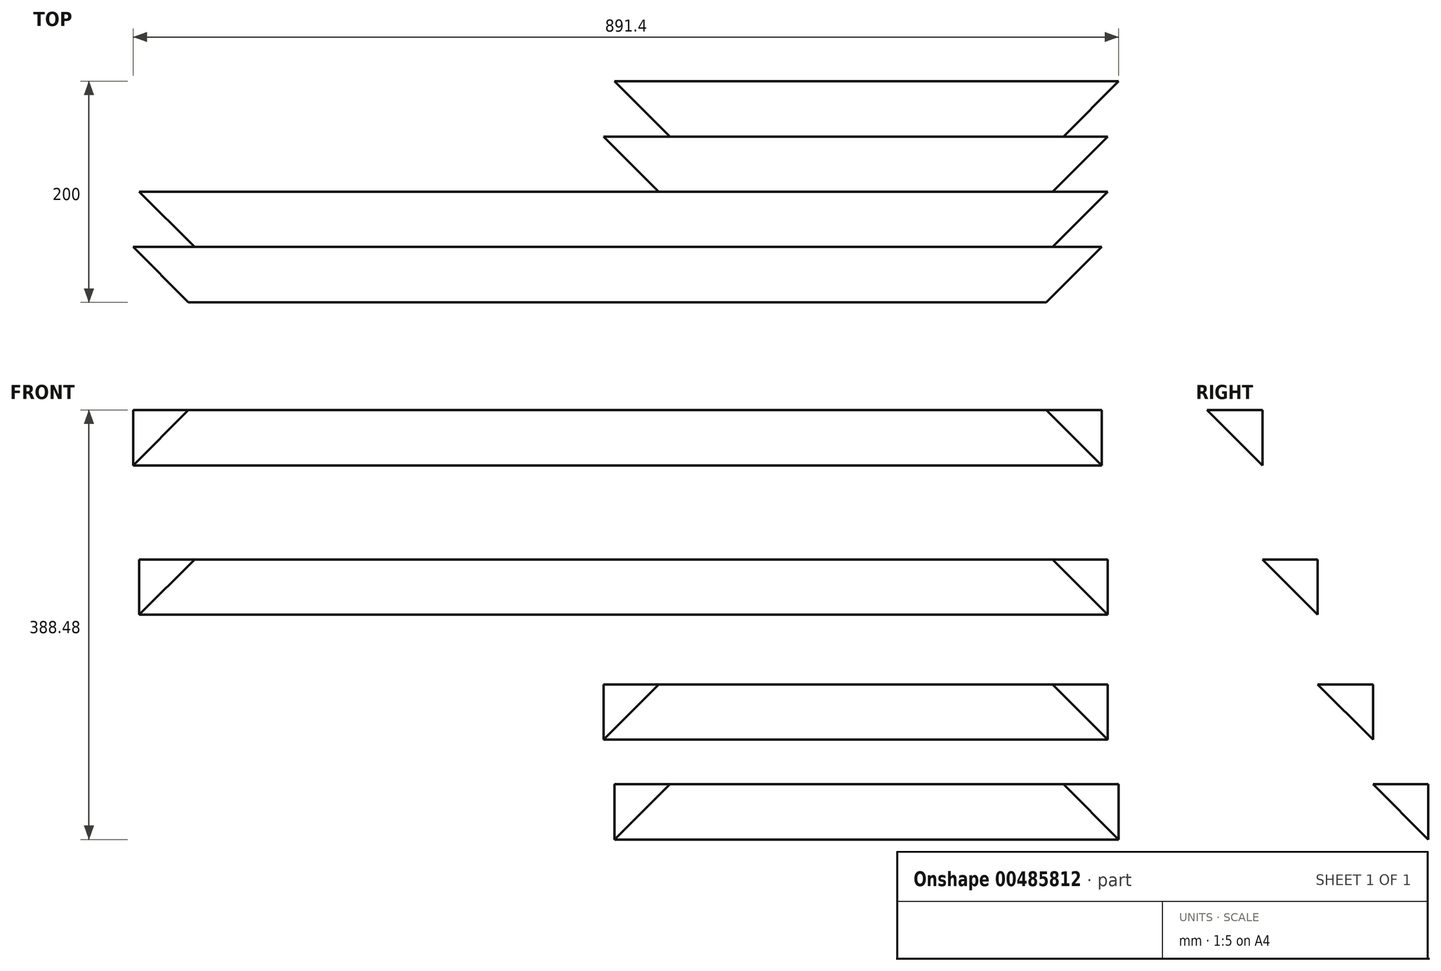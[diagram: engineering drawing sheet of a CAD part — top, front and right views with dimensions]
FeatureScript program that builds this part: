
annotation { "Feature Type Name" : "Feature", "Feature Type Description" : "" }
export const myFeature = defineFeature(function(context is Context, id is Id, definition is map)
    precondition{}
    {
        {
            var Q0;
            Q0=qCreatedBy(makeId("Top.planeOp"),FACE);
            var sketch = newSketch(context, id + "F0", { "sketchPlane" : qUnion([Q0])});
            skLineSegment(sketch, "E0.bottom", {"start": v(-271.54, 58.9) * mm, "end": v(604.46, 58.9) * mm});
            skLineSegment(sketch, "E0.top", {"start": v(-271.54, 8.9) * mm, "end": v(604.46, 8.9) * mm});
            skLineSegment(sketch, "E0.left", {"start": v(-271.54, 58.9) * mm, "end": v(-271.54, 8.9) * mm});
            skLineSegment(sketch, "E0.right", {"start": v(604.46, 58.9) * mm, "end": v(604.46, 8.9) * mm});
            skSolve(sketch);
        }
        {
            var Q0;
            Q0 = qSketchRegion(id + "F0", true);
            extrude(context, id + "F1", {"entities" : qUnion([Q0]), "depth" : 50 * mm});
        }
        {
            var Q0;
            Q0=makeQuery(id+"F1.opExtrude","SWEPT_FACE",FACE,{"disambiguationData":[OSD([sQuery(id+"F0.wireOp",EDGE,"E0.right")])]});
            var sketch = newSketch(context, id + "F2", { "sketchPlane" : qUnion([Q0])});
            skLineSegment(sketch, "E1", {"start": v(8.9, 50) * mm, "end": v(58.9, 0) * mm});
            skLineSegment(sketch, "E2", {"start": v(58.9, 0) * mm, "end": v(8.9, 0) * mm});
            skLineSegment(sketch, "E3", {"start": v(8.9, 0) * mm, "end": v(8.9, 50) * mm});
            skSolve(sketch);
        }
        {
            var Q0;
            Q0 = qSketchRegion(id + "F2", true);
            extrude(context, id + "F3", {"entities" : qUnion([Q0]), "operationType" : NewBodyOperationType.REMOVE, "endBound" : BoundingType.THROUGH_ALL, "oppositeDirection" : true, "depth" : 25 * mm});
        }
        {
            var Q0;
            Q0=makeQuery(id+"F1.opExtrude","SWEPT_FACE",FACE,{"disambiguationData":[OSD([sQuery(id+"F0.wireOp",EDGE,"E0.bottom")])]});
            var sketch = newSketch(context, id + "F4", { "sketchPlane" : qUnion([Q0])});
            skLineSegment(sketch, "E4.bottom", {"start": v(-609.99, -85.16) * mm, "end": v(266.01, -85.16) * mm});
            skLineSegment(sketch, "E4.top", {"start": v(-609.99, -135.16) * mm, "end": v(266.01, -135.16) * mm});
            skLineSegment(sketch, "E4.left", {"start": v(-609.99, -85.16) * mm, "end": v(-609.99, -135.16) * mm});
            skLineSegment(sketch, "E4.right", {"start": v(266.01, -85.16) * mm, "end": v(266.01, -135.16) * mm});
            skSolve(sketch);
        }
        {
            var Q0;
            Q0=makeQuery(id+"F4.imprint","IMPRINT",FACE,{"disambiguationData":[TD([[makeQuery(id+"F4.imprint","IMPRINT",EDGE,{"derivedFrom":sQuery(id+"F4.wireOp",EDGE,"E4.bottom")}),-1.0]])]});
            extrude(context, id + "F5", {"entities" : qUnion([Q0]), "depth" : 50 * mm});
        }
        {
            var Q0;
            Q0=makeQuery(id+"F5.opExtrude","SWEPT_FACE",FACE,{"disambiguationData":[OSD([sQuery(id+"F4.wireOp",EDGE,"E4.left")])]});
            var sketch = newSketch(context, id + "F6", { "sketchPlane" : qUnion([Q0])});
            skLineSegment(sketch, "E5", {"start": v(58.9, -85.16) * mm, "end": v(108.9, -135.16) * mm});
            skLineSegment(sketch, "E6", {"start": v(108.9, -135.16) * mm, "end": v(58.9, -135.16) * mm});
            skLineSegment(sketch, "E7", {"start": v(58.9, -135.16) * mm, "end": v(58.9, -85.16) * mm});
            skSolve(sketch);
        }
        {
            var Q0;
            Q0=makeQuery(id+"F6.imprint","IMPRINT",FACE,{"disambiguationData":[TD([[makeQuery(id+"F6.imprint","IMPRINT",EDGE,{"derivedFrom":sQuery(id+"F6.wireOp",EDGE,"E5")}),-1.0]])]});
            extrude(context, id + "F7", {"entities" : qUnion([Q0]), "operationType" : NewBodyOperationType.REMOVE, "oppositeDirection" : true, "depth" : 876 * mm});
        }
        {
            var Q0;
            Q0=makeQuery(id+"F5.opExtrude","CAP_FACE",FACE,{"disambiguationData":[OSD([sQuery(id+"F4.wireOp",EDGE,"E4.bottom"),sQuery(id+"F4.wireOp",EDGE,"E4.top"),sQuery(id+"F4.wireOp",EDGE,"E4.left"),sQuery(id+"F4.wireOp",EDGE,"E4.right")])],"isStart":false});
            var sketch = newSketch(context, id + "F8", { "sketchPlane" : qUnion([Q0])});
            skLineSegment(sketch, "E8", {"start": v(-609.99, -198.17) * mm, "end": v(-153.99, -198.17) * mm});
            skLineSegment(sketch, "E9", {"start": v(-153.99, -198.17) * mm, "end": v(-153.99, -248.17) * mm});
            skLineSegment(sketch, "E10", {"start": v(-153.99, -248.17) * mm, "end": v(-609.99, -248.17) * mm});
            skLineSegment(sketch, "E11", {"start": v(-609.99, -248.17) * mm, "end": v(-609.99, -198.17) * mm});
            skSolve(sketch);
        }
        {
            var Q0;
            Q0=makeQuery(id+"F8.imprint","IMPRINT",FACE,{"disambiguationData":[TD([[makeQuery(id+"F8.imprint","IMPRINT",EDGE,{"derivedFrom":sQuery(id+"F8.wireOp",EDGE,"E8")}),-1.0]])]});
            extrude(context, id + "F9", {"entities" : qUnion([Q0]), "depth" : 50 * mm});
        }
        {
            var Q0;
            Q0=makeQuery(id+"F9.opExtrude","SWEPT_FACE",FACE,{"disambiguationData":[OSD([sQuery(id+"F8.wireOp",EDGE,"E11")])]});
            var sketch = newSketch(context, id + "F10", { "sketchPlane" : qUnion([Q0])});
            skLineSegment(sketch, "E12", {"start": v(108.9, -198.17) * mm, "end": v(158.9, -248.17) * mm});
            skLineSegment(sketch, "E13", {"start": v(158.9, -248.17) * mm, "end": v(108.9, -248.17) * mm});
            skLineSegment(sketch, "E14", {"start": v(108.9, -248.17) * mm, "end": v(108.9, -198.17) * mm});
            skSolve(sketch);
        }
        {
            var Q0;
            Q0=makeQuery(id+"F10.imprint","IMPRINT",FACE,{"disambiguationData":[TD([[makeQuery(id+"F10.imprint","IMPRINT",EDGE,{"derivedFrom":sQuery(id+"F10.wireOp",EDGE,"E12")}),-1.0]])]});
            extrude(context, id + "F11", {"entities" : qUnion([Q0]), "operationType" : NewBodyOperationType.REMOVE, "oppositeDirection" : true, "depth" : 876 * mm});
        }
        {
            var Q0;
            Q0=makeQuery(id+"F9.opExtrude","CAP_FACE",FACE,{"disambiguationData":[OSD([sQuery(id+"F8.wireOp",EDGE,"E8"),sQuery(id+"F8.wireOp",EDGE,"E9"),sQuery(id+"F8.wireOp",EDGE,"E10"),sQuery(id+"F8.wireOp",EDGE,"E11")])],"isStart":false});
            var sketch = newSketch(context, id + "F12", { "sketchPlane" : qUnion([Q0])});
            skLineSegment(sketch, "E15.bottom", {"start": v(-619.86, -288.48) * mm, "end": v(-163.86, -288.48) * mm});
            skLineSegment(sketch, "E15.top", {"start": v(-619.86, -338.48) * mm, "end": v(-163.86, -338.48) * mm});
            skLineSegment(sketch, "E15.left", {"start": v(-619.86, -288.48) * mm, "end": v(-619.86, -338.48) * mm});
            skLineSegment(sketch, "E15.right", {"start": v(-163.86, -288.48) * mm, "end": v(-163.86, -338.48) * mm});
            skSolve(sketch);
        }
        {
            var Q0;
            Q0=makeQuery(id+"F12.imprint","IMPRINT",FACE,{"disambiguationData":[TD([[makeQuery(id+"F12.imprint","IMPRINT",EDGE,{"derivedFrom":sQuery(id+"F12.wireOp",EDGE,"E15.bottom")}),-1.0]])]});
            extrude(context, id + "F13", {"entities" : qUnion([Q0]), "depth" : 50 * mm});
        }
        {
            var Q0;
            Q0=makeQuery(id+"F13.opExtrude","SWEPT_FACE",FACE,{"disambiguationData":[OSD([sQuery(id+"F12.wireOp",EDGE,"E15.left")])]});
            var sketch = newSketch(context, id + "F14", { "sketchPlane" : qUnion([Q0])});
            skLineSegment(sketch, "E16", {"start": v(158.9, -288.48) * mm, "end": v(208.9, -338.48) * mm});
            skLineSegment(sketch, "E17", {"start": v(208.9, -338.48) * mm, "end": v(158.9, -338.48) * mm});
            skLineSegment(sketch, "E18", {"start": v(158.9, -338.48) * mm, "end": v(158.9, -288.48) * mm});
            skSolve(sketch);
        }
        {
            var Q0;
            Q0=makeQuery(id+"F14.imprint","IMPRINT",FACE,{"disambiguationData":[TD([[makeQuery(id+"F14.imprint","IMPRINT",EDGE,{"derivedFrom":sQuery(id+"F14.wireOp",EDGE,"E16")}),-1.0]])]});
            extrude(context, id + "F15", {"entities" : qUnion([Q0]), "operationType" : NewBodyOperationType.REMOVE, "oppositeDirection" : true, "depth" : 456 * mm});
        }
        {
            var Q0;
            Q0=makeQuery(id+"F1.opExtrude","CAP_FACE",FACE,{"disambiguationData":[OSD([sQuery(id+"F0.wireOp",EDGE,"E0.bottom"),sQuery(id+"F0.wireOp",EDGE,"E0.top"),sQuery(id+"F0.wireOp",EDGE,"E0.left"),sQuery(id+"F0.wireOp",EDGE,"E0.right")])],"isStart":false});
            var sketch = newSketch(context, id + "F16", { "sketchPlane" : qUnion([Q0])});
            skLineSegment(sketch, "E19", {"start": v(-271.54, 58.9) * mm, "end": v(-271.54, 8.9) * mm});
            skLineSegment(sketch, "E20", {"start": v(-271.54, 8.9) * mm, "end": v(-221.54, 8.9) * mm});
            skLineSegment(sketch, "E21", {"start": v(-221.54, 8.9) * mm, "end": v(-271.54, 58.9) * mm});
            skLineSegment(sketch, "E22", {"start": v(604.46, 58.9) * mm, "end": v(604.46, 8.9) * mm});
            skLineSegment(sketch, "E23", {"start": v(604.46, 8.9) * mm, "end": v(554.46, 8.9) * mm});
            skLineSegment(sketch, "E24", {"start": v(554.46, 8.9) * mm, "end": v(604.46, 58.9) * mm});
            skSolve(sketch);
        }
        {
            var Q0;
            Q0 = qSketchRegion(id + "F16", true);
            extrude(context, id + "F17", {"entities" : qUnion([Q0]), "operationType" : NewBodyOperationType.REMOVE, "endBound" : BoundingType.THROUGH_ALL, "oppositeDirection" : true, "depth" : 25 * mm});
        }
        {
            var Q0;
            Q0=makeQuery(id+"F5.opExtrude","SWEPT_FACE",FACE,{"disambiguationData":[OSD([sQuery(id+"F4.wireOp",EDGE,"E4.bottom")])]});
            var sketch = newSketch(context, id + "F18", { "sketchPlane" : qUnion([Q0])});
            skLineSegment(sketch, "E25", {"start": v(-266.01, 108.9) * mm, "end": v(-266.01, 58.9) * mm});
            skLineSegment(sketch, "E26", {"start": v(-266.01, 58.9) * mm, "end": v(-216.01, 58.9) * mm});
            skLineSegment(sketch, "E27", {"start": v(-216.01, 58.9) * mm, "end": v(-266.01, 108.9) * mm});
            skLineSegment(sketch, "E28", {"start": v(609.99, 108.9) * mm, "end": v(609.99, 58.9) * mm});
            skLineSegment(sketch, "E29", {"start": v(609.99, 58.9) * mm, "end": v(559.99, 58.9) * mm});
            skLineSegment(sketch, "E30", {"start": v(559.99, 58.9) * mm, "end": v(609.99, 108.9) * mm});
            skSolve(sketch);
        }
        {
            var Q0;
            Q0 = qSketchRegion(id + "F18", true);
            extrude(context, id + "F19", {"entities" : qUnion([Q0]), "operationType" : NewBodyOperationType.REMOVE, "endBound" : BoundingType.THROUGH_ALL, "oppositeDirection" : true, "depth" : 25 * mm});
        }
        {
            var Q0;
            Q0=makeQuery(id+"F9.opExtrude","SWEPT_FACE",FACE,{"disambiguationData":[OSD([sQuery(id+"F8.wireOp",EDGE,"E8")])]});
            var sketch = newSketch(context, id + "F20", { "sketchPlane" : qUnion([Q0])});
            skLineSegment(sketch, "E31", {"start": v(153.99, 158.9) * mm, "end": v(153.99, 108.9) * mm});
            skLineSegment(sketch, "E32", {"start": v(153.99, 108.9) * mm, "end": v(203.99, 108.9) * mm});
            skLineSegment(sketch, "E33", {"start": v(203.99, 108.9) * mm, "end": v(153.99, 158.9) * mm});
            skLineSegment(sketch, "E34", {"start": v(609.99, 158.9) * mm, "end": v(559.99, 108.9) * mm});
            skLineSegment(sketch, "E35", {"start": v(559.99, 108.9) * mm, "end": v(609.99, 108.9) * mm});
            skLineSegment(sketch, "E36", {"start": v(609.99, 108.9) * mm, "end": v(609.99, 158.9) * mm});
            skSolve(sketch);
        }
        {
            var Q0;
            Q0 = qSketchRegion(id + "F20", true);
            extrude(context, id + "F21", {"entities" : qUnion([Q0]), "operationType" : NewBodyOperationType.REMOVE, "endBound" : BoundingType.THROUGH_ALL, "oppositeDirection" : true, "depth" : 25 * mm});
        }
        {
            var Q0;
            Q0=makeQuery(id+"F13.opExtrude","SWEPT_FACE",FACE,{"disambiguationData":[OSD([sQuery(id+"F12.wireOp",EDGE,"E15.bottom")])]});
            var sketch = newSketch(context, id + "F22", { "sketchPlane" : qUnion([Q0])});
            skLineSegment(sketch, "E37", {"start": v(163.86, 208.9) * mm, "end": v(163.86, 158.9) * mm});
            skLineSegment(sketch, "E38", {"start": v(163.86, 158.9) * mm, "end": v(213.86, 158.9) * mm});
            skLineSegment(sketch, "E39", {"start": v(213.86, 158.9) * mm, "end": v(163.86, 208.9) * mm});
            skLineSegment(sketch, "E40", {"start": v(619.86, 208.9) * mm, "end": v(619.86, 158.9) * mm});
            skLineSegment(sketch, "E41", {"start": v(619.86, 158.9) * mm, "end": v(569.86, 158.9) * mm});
            skLineSegment(sketch, "E42", {"start": v(569.86, 158.9) * mm, "end": v(619.86, 208.9) * mm});
            skSolve(sketch);
        }
        {
            var Q0;
            Q0 = qSketchRegion(id + "F22", true);
            extrude(context, id + "F23", {"entities" : qUnion([Q0]), "operationType" : NewBodyOperationType.REMOVE, "oppositeDirection" : true, "depth" : 50 * mm});
        }
    });
